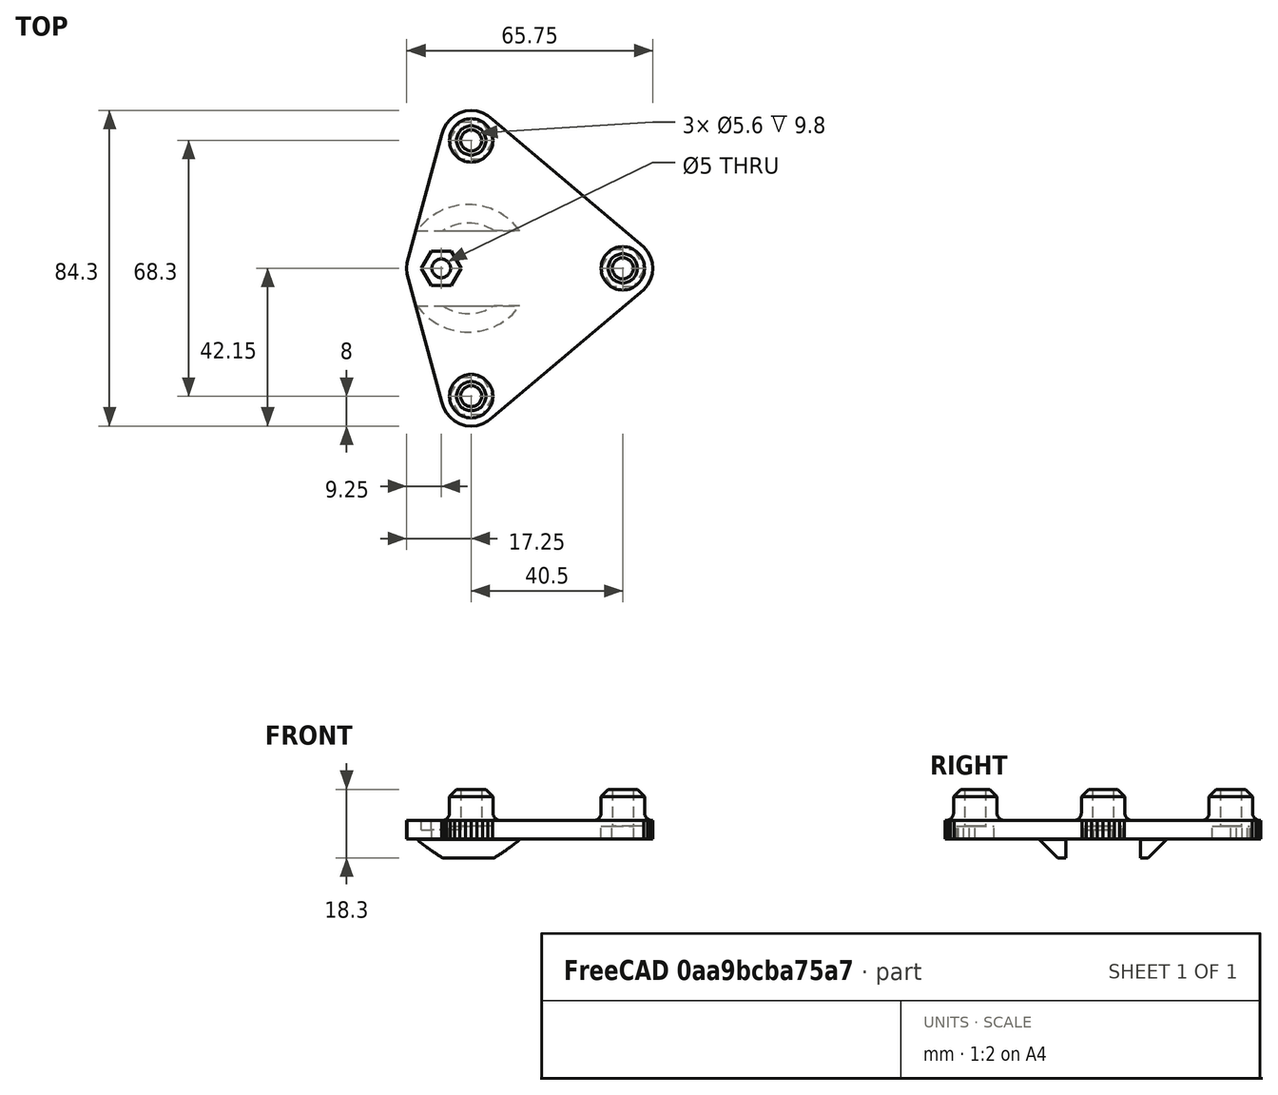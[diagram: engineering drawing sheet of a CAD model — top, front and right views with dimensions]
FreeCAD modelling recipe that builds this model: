
FCSTD DOCUMENT  (FreeCAD 0.19R24267 +99 (Git))
Label: carroZ_3_V2
License: All rights reserved
LicenseURL: http://en.wikipedia.org/wiki/All_rights_reserved
objects: Part::Feature×37, Part::Cylinder×8, Part::Cut×5, Part::Chamfer×5, Part::Part2DObjectPython×4, Part::MultiFuse×4, Part::Prism×4, Part::Box×3, Part::Fillet×3, Part::FeaturePython×2, Part::Extrusion×1, Part::Common×1, App::DocumentObjectGroupPython×1, Part::Refine×1
note: 78 computed .brp shape members not serialized (recipe doc carries the construction recipe); baked Part::Feature solids carry a one-line shape summary decoded from their .brp

FEATURE [Part::Feature] polygon
  shape: bbox 49.75 x 68.3 x 2e-07 mm, 1 faces, 0 solids (baked)
FEATURE [Part::Part2DObjectPython] circle  # Draft 2D object (typed FeaturePython)
  Area = 201.062
  FirstAngle = 0
  LastAngle = 0
  MakeFace = true
  Radius = 8
FEATURE [Part::FeaturePython] minkowski  # WARN: FeaturePython — macro-defined, semantics opaque (R4)
  Arguments = {'convexity': '0'}
  Children = -> [polygon,circle]
  Operation = minkowski
FEATURE [Part::Part2DObjectPython] circle001  # Draft 2D object (typed FeaturePython)
  Area = 24.6301
  FirstAngle = 0
  LastAngle = 0
  MakeFace = true
  Placement = pos=(-20.25,-34.15,0) rot=(0,0,1;0rad)
  Radius = 2.8
FEATURE [Part::Part2DObjectPython] circle002  # Draft 2D object (typed FeaturePython)
  Area = 24.6301
  FirstAngle = 0
  LastAngle = 0
  MakeFace = true
  Placement = pos=(-20.25,34.15,0) rot=(0,0,1;0rad)
  Radius = 2.8
FEATURE [Part::Part2DObjectPython] circle003  # Draft 2D object (typed FeaturePython)
  Area = 24.6301
  FirstAngle = 0
  LastAngle = 0
  MakeFace = true
  Placement = pos=(20.25,0,0) rot=(0,0,1;0rad)
  Radius = 2.8
FEATURE [Part::MultiFuse] union
  Shapes = -> [circle001,circle002,circle003]
FEATURE [Part::Cut] difference
  Base = -> minkowski
  Tool = -> union
FEATURE [Part::FeaturePython] RefineLinearExtrude  # WARN: FeaturePython — macro-defined, semantics opaque (R4)
  Base = -> difference
FEATURE [Part::Extrusion] LinearExtrude
  Base = -> RefineLinearExtrude
  Dir = (0,0,5)
  DirMode = 0
  FaceMakerClass = Part::FaceMakerBullseye
  LengthFwd = 0
  LengthRev = 0
  Solid = false
  Symmetric = false
FEATURE [Part::Cylinder] cylinder
  Angle = 360
  AttacherType = Attacher::AttachEngine3D
  Height = 13.3
  Radius = 5.8
FEATURE [Part::Cylinder] cylinder001
  Angle = 360
  AttacherType = Attacher::AttachEngine3D
  Height = 53.2
  Placement = pos=(0,0,-26.6) rot=(0,0,1;0rad)
  Radius = 2.8
FEATURE [Part::Cut] difference001
  Base = -> cylinder
  Placement = pos=(-20.25,-34.15,0) rot=(0,0,1;0rad)
  Tool = -> cylinder001
FEATURE [Part::Cylinder] cylinder002
  Angle = 360
  AttacherType = Attacher::AttachEngine3D
  Height = 13.3
  Radius = 5.8
FEATURE [Part::Cylinder] cylinder003
  Angle = 360
  AttacherType = Attacher::AttachEngine3D
  Height = 53.2
  Placement = pos=(0,0,-26.6) rot=(0,0,1;0rad)
  Radius = 2.8
FEATURE [Part::Cut] difference002
  Base = -> cylinder002
  Placement = pos=(-20.25,34.15,0) rot=(0,0,1;0rad)
  Tool = -> cylinder003
FEATURE [Part::Cylinder] cylinder004
  Angle = 360
  AttacherType = Attacher::AttachEngine3D
  Height = 13.3
  Radius = 5.8
FEATURE [Part::Cylinder] cylinder005
  Angle = 360
  AttacherType = Attacher::AttachEngine3D
  Height = 53.2
  Placement = pos=(0,0,-26.6) rot=(0,0,1;0rad)
  Radius = 2.8
FEATURE [Part::Cut] difference003
  Base = -> cylinder004
  Placement = pos=(20.25,0,0) rot=(0,0,1;0rad)
  Tool = -> cylinder005
FEATURE [Part::Cylinder] cylinder006
  Angle = 360
  AttacherType = Attacher::AttachEngine3D
  Height = 5
  Placement = pos=(-21,0,0) rot=(1,0,0;3.14159rad)
  Radius = 17
FEATURE [Part::MultiFuse] union001
  Shapes = -> [LinearExtrude,difference001,difference002,difference003,cylinder006]
FEATURE [Part::Prism] prism
  AttacherType = Attacher::AttachEngine3D
  Circumradius = 5.79
  FirstAngle = 0
  Height = 7
  Placement = pos=(-20.25,-34.15,-3.5) rot=(0,0,1;0rad)
  Polygon = 6
  SecondAngle = 0
FEATURE [Part::Prism] prism001
  AttacherType = Attacher::AttachEngine3D
  Circumradius = 5.79
  FirstAngle = 0
  Height = 7
  Placement = pos=(-20.25,34.15,-3.5) rot=(0,0,1;0rad)
  Polygon = 6
  SecondAngle = 0
FEATURE [Part::Prism] prism002
  AttacherType = Attacher::AttachEngine3D
  Circumradius = 5.79
  FirstAngle = 0
  Height = 7
  Placement = pos=(20.25,0,-3.5) rot=(0,0,1;0rad)
  Polygon = 6
  SecondAngle = 0
FEATURE [Part::MultiFuse] Group
  Shapes = -> [prism,prism001,prism002]
FEATURE [Part::Cylinder] cylinder007
  Angle = 360
  AttacherType = Attacher::AttachEngine3D
  Height = 100
  Placement = pos=(-28.25,0,-47.5) rot=(0,0,1;0rad)
  Radius = 2.5
FEATURE [Part::Prism] prism003
  AttacherType = Attacher::AttachEngine3D
  Circumradius = 5.29
  FirstAngle = 0
  Height = 100
  Placement = pos=(-28.25,0,2.5) rot=(0,0,1;0rad)
  Polygon = 6
  SecondAngle = 0
FEATURE [Part::Box] cube
  AttacherType = Attacher::AttachEngine3D
  Height = 20
  Length = 30
  Placement = pos=(-40,-10,-20) rot=(0,0,1;0rad)
  Width = 20
FEATURE [Part::Box] cube001
  AttacherType = Attacher::AttachEngine3D
  Height = 20
  Length = 30
  Placement = pos=(-30,-10,-20) rot=(0,0,1;0rad)
  Width = 20
FEATURE [Part::MultiFuse] union002
  Shapes = -> [Group,cylinder007,prism003,cube,cube001]
FEATURE [Part::Cut] difference004
  Base = -> union001
  Tool = -> union002
FEATURE [Part::Box] cube002
  AttacherType = Attacher::AttachEngine3D
  Height = 200
  Length = 200
  Placement = pos=(-100,-100,-100) rot=(0,0,1;0rad)
  Width = 200
FEATURE [Part::Common] intersection
  Base = -> difference004
  Tool = -> cube002
FEATURE [App::DocumentObjectGroupPython] LayerContainer  label="Capas"  # scripted group (container) (typed FeaturePython)
FEATURE [Part::Feature] Line
  shape: bbox 1.561 x 0.1533 x 2e-07 mm, 0 faces, 0 solids (baked)
FEATURE [Part::Feature] Line001
  shape: bbox 1.561 x 0.1533 x 2e-07 mm, 0 faces, 0 solids (baked)
FEATURE [Part::Feature] Line002
  shape: bbox 1.501 x 0.4561 x 2e-07 mm, 0 faces, 0 solids (baked)
FEATURE [Part::Feature] Line003
  shape: bbox 1.383 x 0.7392 x 2e-07 mm, 0 faces, 0 solids (baked)
FEATURE [Part::Feature] Line004
  shape: bbox 1.213 x 0.9942 x 2e-07 mm, 0 faces, 0 solids (baked)
FEATURE [Part::Feature] Line005
  shape: bbox 0.9942 x 1.213 x 2e-07 mm, 0 faces, 0 solids (baked)
FEATURE [Part::Feature] Line006
  shape: bbox 0.7392 x 1.383 x 2e-07 mm, 0 faces, 0 solids (baked)
FEATURE [Part::Feature] Line007
  shape: bbox 0.4561 x 1.501 x 2e-07 mm, 0 faces, 0 solids (baked)
FEATURE [Part::Feature] Line008
  shape: bbox 9.25 x 34.15 x 2e-07 mm, 0 faces, 0 solids (baked)
FEATURE [Part::Feature] Line009
  shape: bbox 0.1533 x 1.561 x 2e-07 mm, 0 faces, 0 solids (baked)
FEATURE [Part::Feature] Line010
  shape: bbox 0.1533 x 1.561 x 2e-07 mm, 0 faces, 0 solids (baked)
FEATURE [Part::Feature] Line011
  shape: bbox 9.25 x 34.15 x 2e-07 mm, 0 faces, 0 solids (baked)
FEATURE [Part::Feature] Line012
  shape: bbox 0.4561 x 1.501 x 2e-07 mm, 0 faces, 0 solids (baked)
FEATURE [Part::Feature] Line013
  shape: bbox 0.7392 x 1.383 x 2e-07 mm, 0 faces, 0 solids (baked)
FEATURE [Part::Feature] Line014
  shape: bbox 0.9942 x 1.213 x 2e-07 mm, 0 faces, 0 solids (baked)
FEATURE [Part::Feature] Line015
  shape: bbox 1.213 x 0.9942 x 2e-07 mm, 0 faces, 0 solids (baked)
FEATURE [Part::Feature] Line016
  shape: bbox 1.383 x 0.7392 x 2e-07 mm, 0 faces, 0 solids (baked)
FEATURE [Part::Feature] Line017
  shape: bbox 1.501 x 0.4561 x 2e-07 mm, 0 faces, 0 solids (baked)
FEATURE [Part::Feature] Line018
  shape: bbox 1.561 x 0.1533 x 2e-07 mm, 0 faces, 0 solids (baked)
FEATURE [Part::Feature] Line019
  shape: bbox 1.561 x 0.1533 x 2e-07 mm, 0 faces, 0 solids (baked)
FEATURE [Part::Feature] Line020
  shape: bbox 1.501 x 0.4561 x 2e-07 mm, 0 faces, 0 solids (baked)
FEATURE [Part::Feature] Line021
  shape: bbox 1.383 x 0.7392 x 2e-07 mm, 0 faces, 0 solids (baked)
FEATURE [Part::Feature] Line022
  shape: bbox 1.213 x 0.9942 x 2e-07 mm, 0 faces, 0 solids (baked)
FEATURE [Part::Feature] Line023
  shape: bbox 40.5 x 34.15 x 2e-07 mm, 0 faces, 0 solids (baked)
FEATURE [Part::Feature] Line024
  shape: bbox 0.9942 x 1.213 x 2e-07 mm, 0 faces, 0 solids (baked)
FEATURE [Part::Feature] Line025
  shape: bbox 0.7392 x 1.383 x 2e-07 mm, 0 faces, 0 solids (baked)
FEATURE [Part::Feature] Line026
  shape: bbox 0.4561 x 1.501 x 2e-07 mm, 0 faces, 0 solids (baked)
FEATURE [Part::Feature] Line027
  shape: bbox 0.1533 x 1.561 x 2e-07 mm, 0 faces, 0 solids (baked)
FEATURE [Part::Feature] Line028
  shape: bbox 0.1533 x 1.561 x 2e-07 mm, 0 faces, 0 solids (baked)
FEATURE [Part::Feature] Line029
  shape: bbox 0.4561 x 1.501 x 2e-07 mm, 0 faces, 0 solids (baked)
FEATURE [Part::Feature] Line030
  shape: bbox 0.7392 x 1.383 x 2e-07 mm, 0 faces, 0 solids (baked)
FEATURE [Part::Feature] Line031
  shape: bbox 0.9942 x 1.213 x 2e-07 mm, 0 faces, 0 solids (baked)
FEATURE [Part::Feature] Line032
  shape: bbox 40.5 x 34.15 x 2e-07 mm, 0 faces, 0 solids (baked)
FEATURE [Part::Feature] Line033
  shape: bbox 1.213 x 0.9942 x 2e-07 mm, 0 faces, 0 solids (baked)
FEATURE [Part::Feature] Line034
  shape: bbox 1.383 x 0.7392 x 2e-07 mm, 0 faces, 0 solids (baked)
FEATURE [Part::Feature] Line035
  shape: bbox 1.501 x 0.4561 x 2e-07 mm, 0 faces, 0 solids (baked)
FEATURE [Part::Refine] intersection001
  Source = -> intersection
FEATURE [Part::Chamfer] Chamfer
  Base = -> intersection001
  Edges = 1 edges r=4.9: [Edge166]
FEATURE [Part::Chamfer] Chamfer001
  Base = -> Chamfer
  Edges = 1 edges r=4.9: [Edge144]
FEATURE [Part::Chamfer] Chamfer002
  Base = -> Chamfer001
  Edges = 1 edges r=1.9: [Edge205]
FEATURE [Part::Chamfer] Chamfer003
  Base = -> Chamfer002
  Edges = 1 edges r=1.9: [Edge138]
FEATURE [Part::Chamfer] Chamfer004
  Base = -> Chamfer003
  Edges = 1 edges r=1.9: [Edge138]
FEATURE [Part::Fillet] Fillet
  Base = -> Chamfer004
  Edges = 1 edges r=2: [Edge42]
FEATURE [Part::Fillet] Fillet001
  Base = -> Fillet
  Edges = 1 edges r=2: [Edge45]
FEATURE [Part::Fillet] Fillet002
  Base = -> Fillet001
  Edges = 1 edges r=2: [Edge45]
